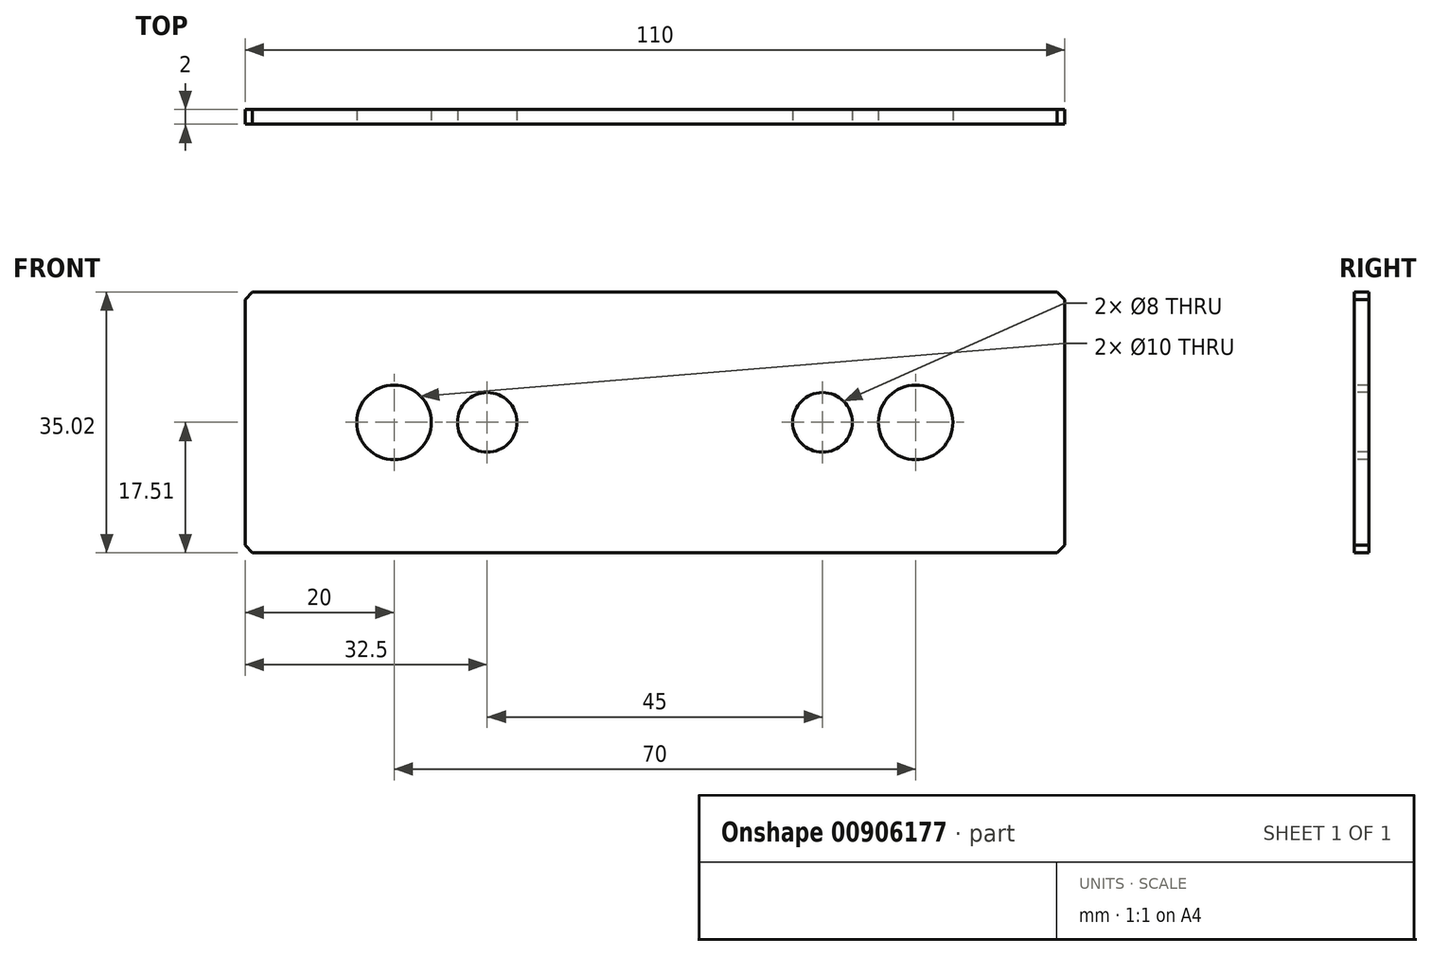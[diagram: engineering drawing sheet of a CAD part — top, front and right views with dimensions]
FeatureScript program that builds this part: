
annotation { "Feature Type Name" : "Feature", "Feature Type Description" : "" }
export const myFeature = defineFeature(function(context is Context, id is Id, definition is map)
    precondition{}
    {
        {
            var Q0;
            Q0=qCreatedBy(makeId("Front.planeOp"),FACE);
            var sketch = newSketch(context, id + "F0", { "sketchPlane" : qUnion([Q0])});
            skLineSegment(sketch, "E0.bottom", {"start": v(-55, -17.5) * mm, "end": v(55, -17.5) * mm});
            skLineSegment(sketch, "E0.top", {"start": v(-55, 17.5) * mm, "end": v(55, 17.5) * mm});
            skLineSegment(sketch, "E0.left", {"start": v(-55, -17.5) * mm, "end": v(-55, 17.5) * mm});
            skLineSegment(sketch, "E0.right", {"start": v(55, -17.5) * mm, "end": v(55, 17.5) * mm});
            skPoint(sketch, "E0.middle", {"position": v(0, 0) * mm});
            skCircle(sketch, "E1", {"center": v(-22.5, 0) * mm, "radius": 4 * mm});
            skCircle(sketch, "E2", {"center": v(22.5, 0) * mm, "radius": 4 * mm});
            skLineSegment(sketch, "E3", {"start": v(-22.5, 0) * mm, "end": v(0, 0) * mm});
            skLineSegment(sketch, "E4", {"start": v(22.5, 0) * mm, "end": v(0, 0) * mm});
            skCircle(sketch, "E5", {"center": v(-35, 0) * mm, "radius": 5 * mm});
            skCircle(sketch, "E6", {"center": v(35, 0) * mm, "radius": 5 * mm});
            skLineSegment(sketch, "E7", {"start": v(-35, 0) * mm, "end": v(0, 0) * mm});
            skLineSegment(sketch, "E8", {"start": v(35, 0) * mm, "end": v(0, 0) * mm});
            skLineSegment(sketch, "E9.bottom", {"start": v(-45, -17.5) * mm, "end": v(45, -17.5) * mm});
            skLineSegment(sketch, "E9.top", {"start": v(-45, 17.5) * mm, "end": v(45, 17.5) * mm});
            skLineSegment(sketch, "E9.left", {"start": v(-45, -17.5) * mm, "end": v(-45, 17.5) * mm});
            skLineSegment(sketch, "E9.right", {"start": v(45, -17.5) * mm, "end": v(45, 17.5) * mm});
            skSolve(sketch);
        }
        {
            var Q0;
            Q0=qSketchRegion(id+"F0",true);
            extrude(context, id + "F1", {"entities" : qUnion([Q0]), "oppositeDirection" : true, "depth" : 2 * mm, "offsetDistance" : 25 * mm});
        }
        {
            var Q0;
            Q0=makeQuery(id+"F1.opExtrude","SWEPT_EDGE",EDGE,{"disambiguationData":[OSD([sQuery(id+"F0.wireOp",EDGE,"E0.top"),sQuery(id+"F0.wireOp",EDGE,"E0.right")])]});
            var Q1;
            Q1=makeQuery(id+"F1.opExtrude","SWEPT_EDGE",EDGE,{"disambiguationData":[OSD([sQuery(id+"F0.wireOp",EDGE,"E0.bottom"),sQuery(id+"F0.wireOp",EDGE,"E0.right")])]});
            var Q2;
            Q2=makeQuery(id+"F1.opExtrude","SWEPT_EDGE",EDGE,{"disambiguationData":[OSD([sQuery(id+"F0.wireOp",EDGE,"E0.bottom"),sQuery(id+"F0.wireOp",EDGE,"E0.left")])]});
            var Q3;
            Q3=makeQuery(id+"F1.opExtrude","SWEPT_EDGE",EDGE,{"disambiguationData":[OSD([sQuery(id+"F0.wireOp",EDGE,"E0.top"),sQuery(id+"F0.wireOp",EDGE,"E0.left")])]});
            chamfer(context, id + "F2", {"entities" : qUnion([Q0, Q1, Q2, Q3]), "width" : 1 * mm, "tangentPropagation" : true});
        }
    });
